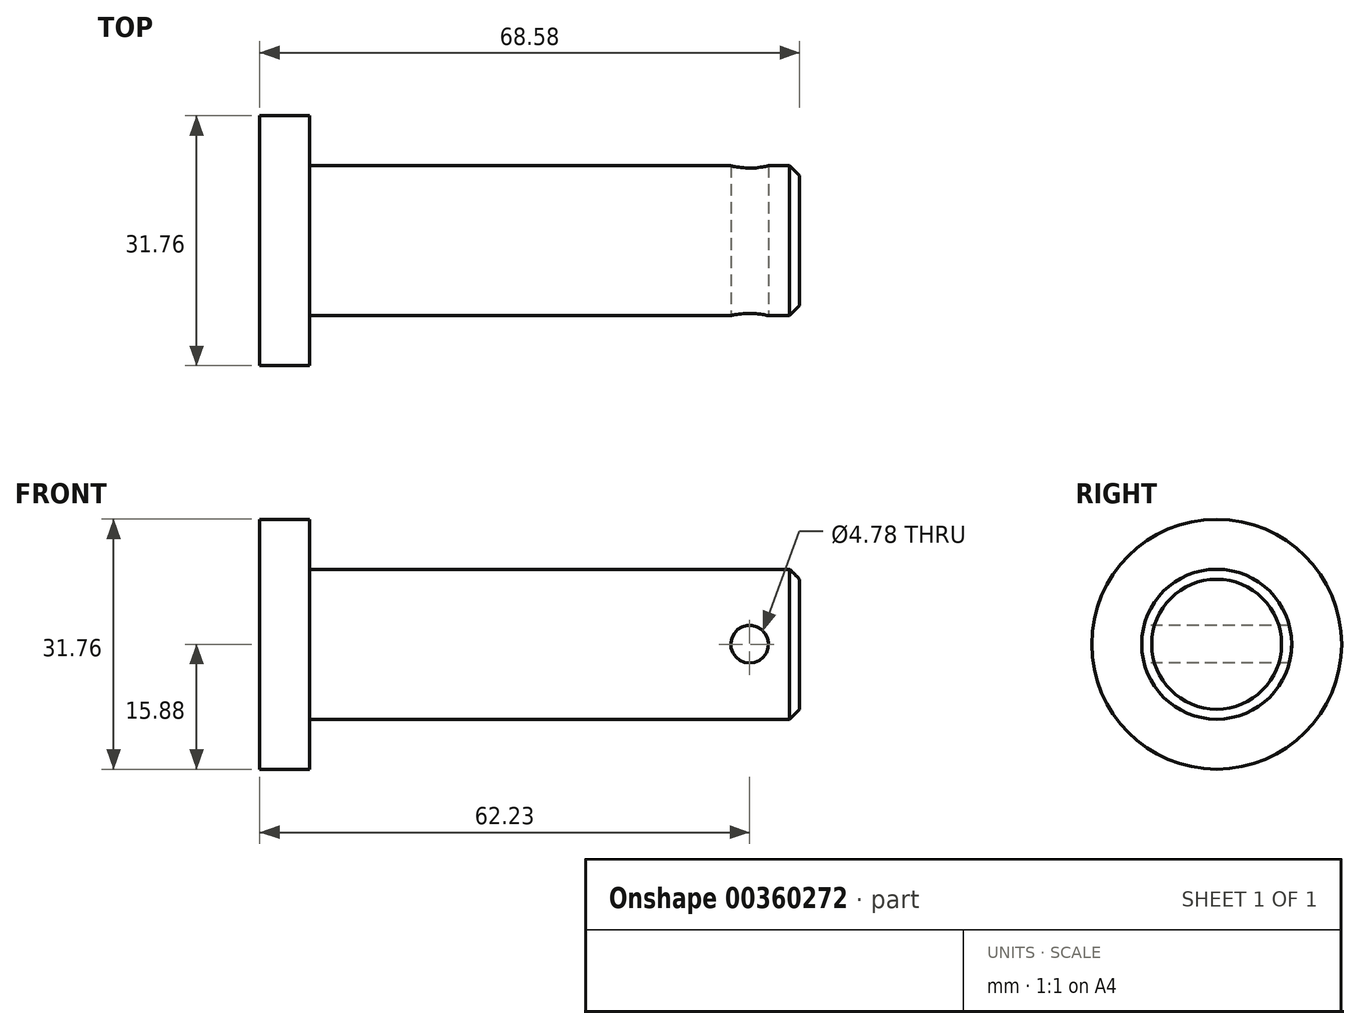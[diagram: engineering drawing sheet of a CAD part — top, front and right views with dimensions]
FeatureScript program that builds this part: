
annotation { "Feature Type Name" : "Feature", "Feature Type Description" : "" }
export const myFeature = defineFeature(function(context is Context, id is Id, definition is map)
    precondition{}
    {
        {
            var Q0;
            Q0=qCreatedBy(makeId("Front.planeOp"),FACE);
            var sketch = newSketch(context, id + "F0", { "sketchPlane" : qUnion([Q0])});
            skLineSegment(sketch, "E0.bottom", {"start": v(0, 0) * mm, "end": v(6.35, 0) * mm});
            skLineSegment(sketch, "E0.top", {"start": v(0, 15.88) * mm, "end": v(6.35, 15.88) * mm});
            skLineSegment(sketch, "E0.left", {"start": v(0, 0) * mm, "end": v(0, 15.88) * mm});
            skLineSegment(sketch, "E0.right", {"start": v(6.35, 0) * mm, "end": v(6.35, 15.88) * mm});
            skLineSegment(sketch, "E1", {"start": v(0, 0) * mm, "end": v(68.58, 0) * mm, "construction": true});
            skPoint(sketch, "E1.endSnap0", {"position": v(3.18, 0) * mm});
            skLineSegment(sketch, "E2", {"start": v(6.35, 0) * mm, "end": v(68.58, 0) * mm});
            skLineSegment(sketch, "E3", {"start": v(68.58, 9.52) * mm, "end": v(6.35, 9.52) * mm});
            skLineSegment(sketch, "E4", {"start": v(68.58, 0) * mm, "end": v(68.58, 9.53) * mm});
            skSolve(sketch);
        }
        {
            var Q0;
            {var subQ1=sQuery(id+"F0.wireOp",EDGE,"E0.bottom");Q0=makeQuery(id+"F0.imprint","IMPRINT",FACE,{"disambiguationData":[TD([[makeQuery(id+"F0.imprint","IMPRINT",EDGE,{"derivedFrom":subQ1}),1.0]])]});}
            var Q1;
            {var subQ0=sQuery(id+"F0.wireOp",EDGE,"E2");Q1=makeQuery(id+"F0.imprint","IMPRINT",FACE,{"disambiguationData":[TD([[makeQuery(id+"F0.imprint","IMPRINT",EDGE,{"derivedFrom":subQ0}),1.0]])]});}
            var Q2;
            Q2=sQuery(id+"F0.wireOp",EDGE,"E2");
            revolve(context, id + "F1", {"entities" : qUnion([Q0, Q1]), "axis" : qUnion([Q2]), "revolveType" : RevolveType.FULL});
        }
        {
            var Q0;
            Q0=makeQuery(id+"F1.opRevolve","SWEPT_EDGE",EDGE,{"disambiguationData":[OSD([sQuery(id+"F0.wireOp",EDGE,"E3"),sQuery(id+"F0.wireOp",EDGE,"E4")])]});
            chamfer(context, id + "F2", {"entities" : qUnion([Q0]), "width" : 1.27 * mm, "tangentPropagation" : true});
        }
        {
            var Q0;
            Q0=qCreatedBy(makeId("Front.planeOp"),FACE);
            var sketch = newSketch(context, id + "F3", { "sketchPlane" : qUnion([Q0])});
            skLineSegment(sketch, "E5", {"start": v(6.35, 9.52) * mm, "end": v(67.31, 9.52) * mm});
            skLineSegment(sketch, "E6", {"start": v(67.31, -9.52) * mm, "end": v(6.35, -9.52) * mm});
            skCircle(sketch, "E7", {"center": v(62.23, 0) * mm, "radius": 2.39 * mm});
            skSolve(sketch);
        }
        {
            var Q0;
            Q0 = qSketchRegion(id + "F3", true);
            extrude(context, id + "F4", {"entities" : qUnion([Q0]), "operationType" : NewBodyOperationType.REMOVE, "oppositeDirection" : true, "depth" : 48.77 * mm, "symmetric" : true});
        }
    });
